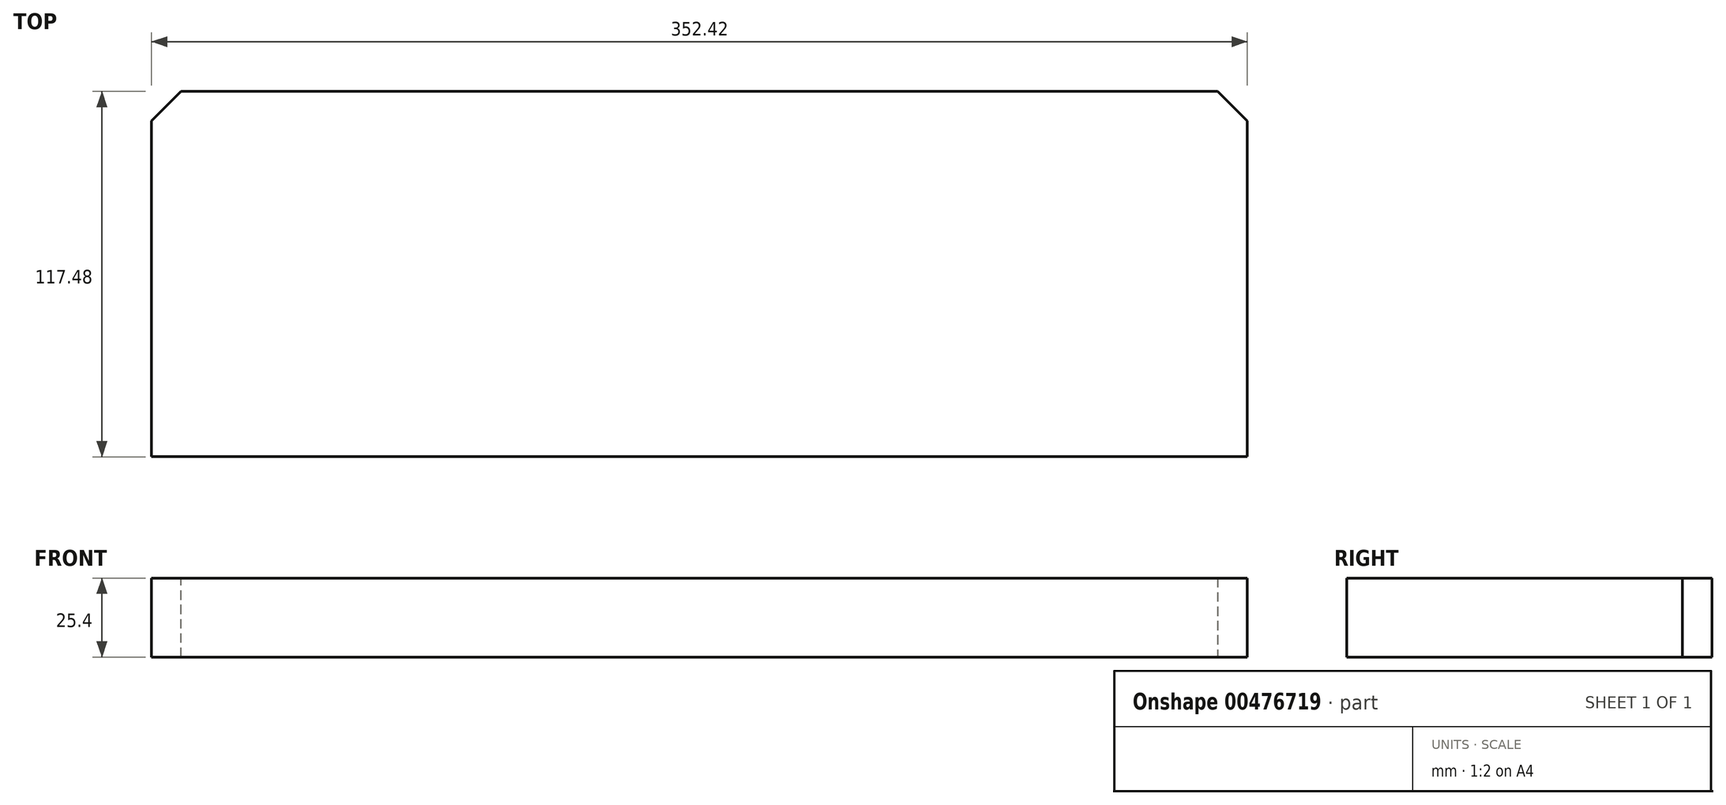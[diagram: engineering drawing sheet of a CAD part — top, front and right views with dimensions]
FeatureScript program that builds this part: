
annotation { "Feature Type Name" : "Feature", "Feature Type Description" : "" }
export const myFeature = defineFeature(function(context is Context, id is Id, definition is map)
    precondition{}
    {
        {
            var Q0;
            Q0=qCreatedBy(makeId("Top.planeOp"),FACE);
            var sketch = newSketch(context, id + "F0", { "sketchPlane" : qUnion([Q0])});
            skLineSegment(sketch, "E0.bottom", {"start": v(176.21, 58.74) * mm, "end": v(-176.21, 58.74) * mm});
            skLineSegment(sketch, "E0.top", {"start": v(176.21, -58.74) * mm, "end": v(-176.21, -58.74) * mm});
            skLineSegment(sketch, "E0.left", {"start": v(176.21, 58.74) * mm, "end": v(176.21, -58.74) * mm});
            skLineSegment(sketch, "E0.right", {"start": v(-176.21, 58.74) * mm, "end": v(-176.21, -58.74) * mm});
            skPoint(sketch, "E0.middle", {"position": v(0, 0) * mm});
            skSolve(sketch);
        }
        {
            var Q0;
            Q0=makeQuery(id+"F0.imprint","IMPRINT",FACE,{"disambiguationData":[TD([[makeQuery(id+"F0.imprint","IMPRINT",EDGE,{"derivedFrom":sQuery(id+"F0.wireOp",EDGE,"E0.bottom")}),1.0]])]});
            extrude(context, id + "F1", {"entities" : qUnion([Q0]), "depth" : 25.4 * mm});
        }
        {
            var Q0;
            Q0=makeQuery(id+"F1.opExtrude","SWEPT_EDGE",EDGE,{"disambiguationData":[OSD([sQuery(id+"F0.wireOp",EDGE,"E0.bottom"),sQuery(id+"F0.wireOp",EDGE,"E0.left")])]});
            var Q1;
            Q1=makeQuery(id+"F1.opExtrude","SWEPT_EDGE",EDGE,{"disambiguationData":[OSD([sQuery(id+"F0.wireOp",EDGE,"E0.bottom"),sQuery(id+"F0.wireOp",EDGE,"E0.right")])]});
            chamfer(context, id + "F2", {"entities" : qUnion([Q0, Q1]), "width" : 9.52 * mm, "tangentPropagation" : true});
        }
    });
